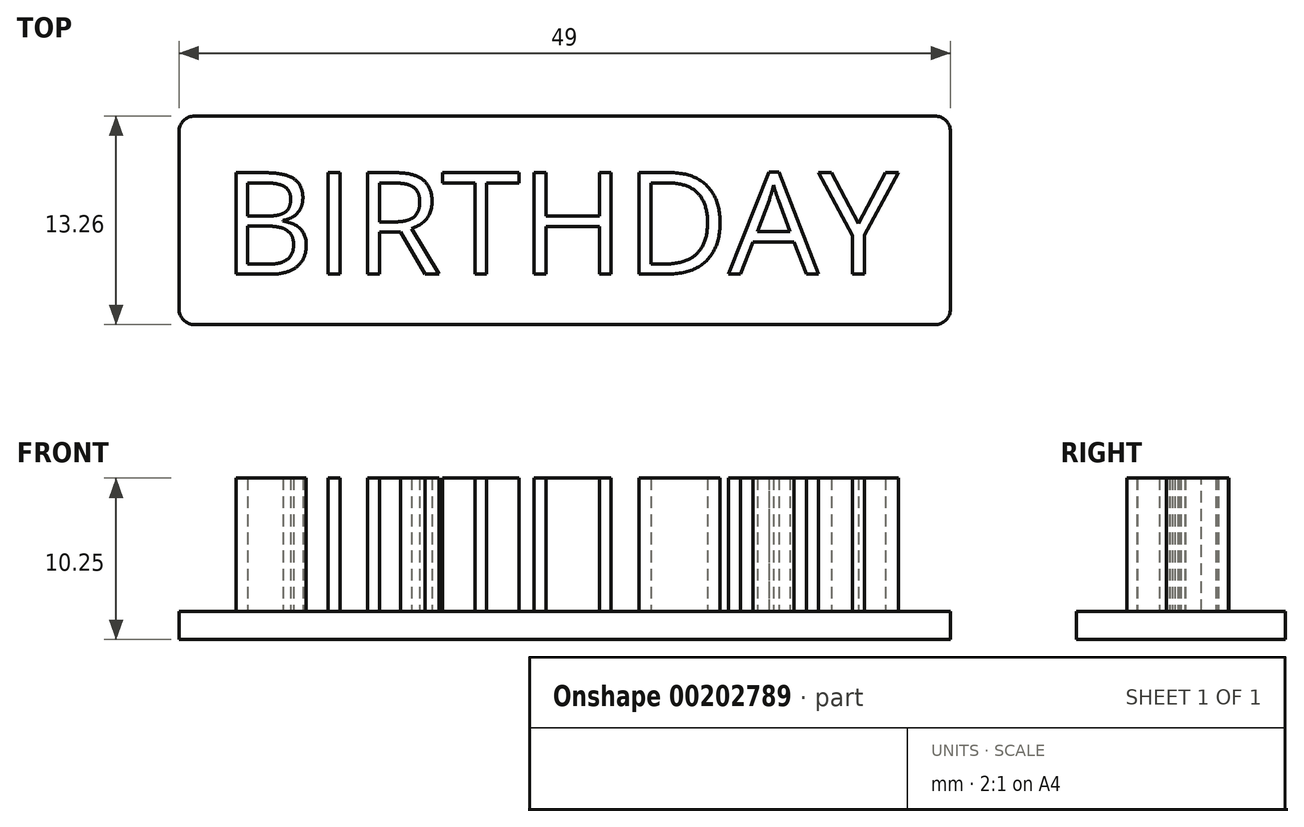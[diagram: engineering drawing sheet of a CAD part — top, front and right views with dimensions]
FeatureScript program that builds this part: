
annotation { "Feature Type Name" : "Feature", "Feature Type Description" : "" }
export const myFeature = defineFeature(function(context is Context, id is Id, definition is map)
    precondition{}
    {
        {
            var Q0;
            Q0=qCreatedBy(makeId("Top.planeOp"),FACE);
            var sketch = newSketch(context, id + "F0", { "sketchPlane" : qUnion([Q0])});
            skLineSegment(sketch, "E0.bottom", {"start": v(23.5, 6.63) * mm, "end": v(-23.5, 6.63) * mm});
            skLineSegment(sketch, "E0.top", {"start": v(23.5, -6.62) * mm, "end": v(-23.5, -6.62) * mm});
            skLineSegment(sketch, "E0.left", {"start": v(24.5, 5.63) * mm, "end": v(24.5, -5.62) * mm});
            skLineSegment(sketch, "E0.right", {"start": v(-24.5, 5.63) * mm, "end": v(-24.5, -5.62) * mm});
            skPoint(sketch, "E0.middle", {"position": v(0, 0) * mm});
            skPoint(sketch, "E1.visualSharp", {"position": v(-24.5, 6.63) * mm});
            skArc(sketch, "E1.filletArc", {"start": v(-23.5, 6.63) * mm, "mid": v(-24.2, 6.33) * mm, "end": v(-24.5, 5.63) * mm});
            skPoint(sketch, "E2.visualSharp", {"position": v(-24.5, -6.62) * mm});
            skArc(sketch, "E2.filletArc", {"start": v(-24.5, -5.62) * mm, "mid": v(-24.2, -6.33) * mm, "end": v(-23.5, -6.62) * mm});
            skPoint(sketch, "E3.visualSharp", {"position": v(24.5, -6.62) * mm});
            skArc(sketch, "E3.filletArc", {"start": v(23.5, -6.62) * mm, "mid": v(24.2, -6.33) * mm, "end": v(24.5, -5.62) * mm});
            skPoint(sketch, "E4.visualSharp", {"position": v(24.5, 6.63) * mm});
            skArc(sketch, "E4.filletArc", {"start": v(24.5, 5.63) * mm, "mid": v(24.2, 6.33) * mm, "end": v(23.5, 6.63) * mm});
            skSolve(sketch);
        }
        {
            var Q0;
            Q0=makeQuery(id+"F0.imprint","IMPRINT",FACE,{"disambiguationData":[TD([[makeQuery(id+"F0.imprint","IMPRINT",EDGE,{"derivedFrom":sQuery(id+"F0.wireOp",EDGE,"E0.bottom")}),1.0]])]});
            extrude(context, id + "F1", {"entities" : qUnion([Q0]), "depth" : 1.8 * mm});
        }
        {
            var Q0;
            Q0=makeQuery(id+"F1.opExtrude","CAP_FACE",FACE,{"disambiguationData":[OSD([sQuery(id+"F0.wireOp",EDGE,"E0.bottom"),sQuery(id+"F0.wireOp",EDGE,"E0.top"),sQuery(id+"F0.wireOp",EDGE,"E0.left"),sQuery(id+"F0.wireOp",EDGE,"E0.right"),sQuery(id+"F0.wireOp",EDGE,"E1.filletArc"),sQuery(id+"F0.wireOp",EDGE,"E2.filletArc"),sQuery(id+"F0.wireOp",EDGE,"E3.filletArc"),sQuery(id+"F0.wireOp",EDGE,"E4.filletArc")])],"isStart":false});
            var sketch = newSketch(context, id + "F2", { "sketchPlane" : qUnion([Q0])});
            skText(sketch, "E5", { "text": "BIRTHDAY", "fontName": "OpenSans-Regular.ttf"});
            const initialGuessF2  = {"E5": [-0.02177, -0.00342, 1, 0, 0.0065]};
            skSetInitialGuess(sketch, initialGuessF2);
            skSolve(sketch);
        }
        {
            var Q0;
            Q0 = qSketchRegion(id + "F2", true);
            extrude(context, id + "F3", {"entities" : qUnion([Q0]), "operationType" : NewBodyOperationType.ADD, "depth" : 8.45 * mm});
        }
    });
